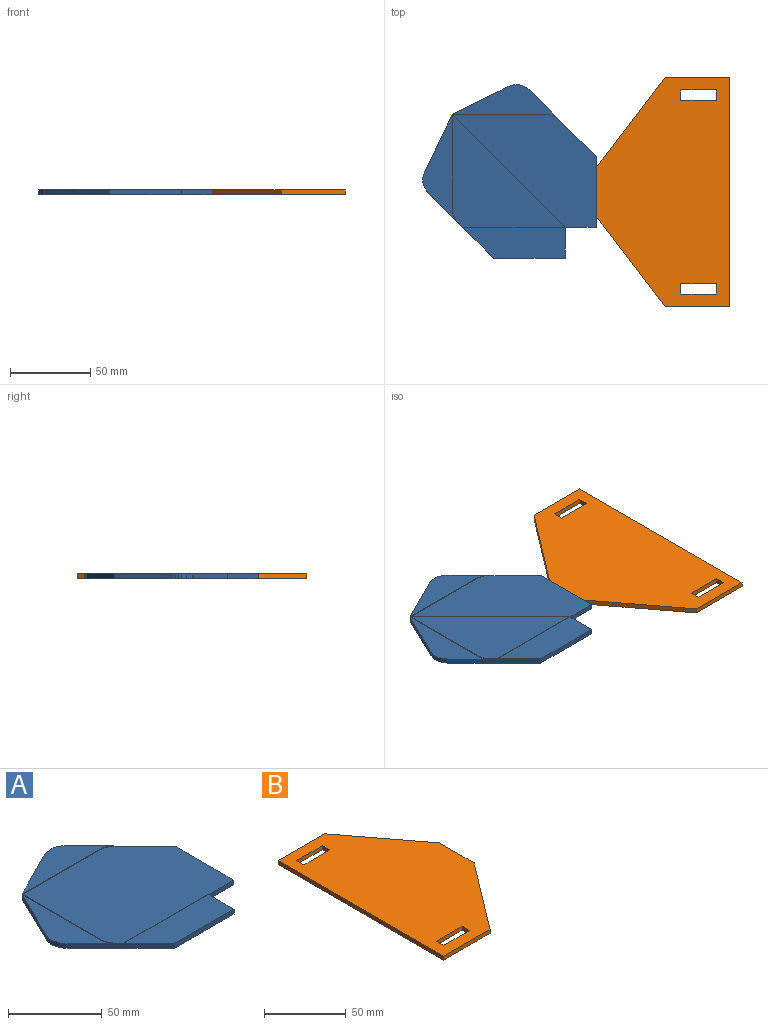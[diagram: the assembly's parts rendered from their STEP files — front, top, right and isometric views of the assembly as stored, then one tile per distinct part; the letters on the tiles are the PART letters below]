
ASSEMBLY  parts=2 mates=1
PART A: 45 faces, bbox 108x108x3.5 mm
  f0: plane 66.76x21.29mm, normal (0,0,1), area 652.9mm2, adj f1,f20,f21,f22,f23,f24,f25,f26
  f1: plane 21.32x21.32mm, normal (-0.71,-0.71,0), area 93mm2, adj f0,f2,f27,f29,f37,f38,f43
  f2: plane 19.19x19.19mm, normal (-0.71,-0.71,0), area 88.2mm2, adj f1,f3,f29,f44
  f3: plane 44.78x3.25mm, normal (0,-1,0), area 145.5mm2, adj f2,f4,f29,f44
  f4: plane 19.19x3.25mm, normal (1,0,0), area 62.4mm2, adj f3,f5,f29,f39,f44
  f5: plane 19.19x3mm, normal (0,-1,0), area 57.6mm2, adj f4,f6,f28,f29
  f6: plane 44.07x3mm, normal (1,0,0), area 132.2mm2, adj f5,f7,f28,f29
  f7: plane 22.74x22.74mm, normal (0.71,0.71,0), area 96.5mm2, adj f6,f8,f28,f29
  f8: plane 3x0.53mm, normal (0.71,0.71,0), area 2.3mm2, adj f7,f9,f28,f29
  f9: plane 17.95x17.94mm, normal (0.71,0.71,0), area 88.8mm2, adj f8,f10,f29,f30,f35
  f10: plane 3.5x0.34mm, normal (0.71,0.71,0), area 1.7mm2, adj f9,f11,f29,f35
  f11: plane 3.5x1.16mm, normal (0.61,0.79,0), area 5.1mm2, adj f10,f12,f29,f35
  f12: plane 3.5x1.95mm, normal (0.51,0.86,0), area 7.9mm2, adj f11,f13,f29,f35
  f13: plane 3.5x2.17mm, normal (0.36,0.93,0), area 8.2mm2, adj f12,f14,f29,f35
  f14: plane 3.5x1.65mm, normal (0.19,0.98,0), area 5.9mm2, adj f13,f15,f29,f35
  f15: plane 3.5x1.43mm, normal (0,1,0), area 5mm2, adj f14,f16,f29,f35
  f16: plane 3.5x2.65mm, normal (-0.13,0.99,0), area 9.4mm2, adj f15,f17,f29,f35
  f17: plane 3.5x2.49mm, normal (-0.32,0.95,0), area 9.2mm2, adj f16,f18,f29,f35
  f18: plane 3.5x0.4mm, normal (-0.51,0.86,0), area 1.6mm2, adj f17,f19,f29,f35
  f19: plane 34.11x17.06mm, normal (-0.45,0.89,0), area 133.5mm2, adj f18,f20,f28,f29,f31,f35,f39,f40
  f20: plane 35.54x17.06mm, normal (-0.9,0.43,0), area 118.3mm2, adj f0,f19,f21,f29
  f21: plane 3x0.3mm, normal (-0.91,0.41,0), area 1mm2, adj f0,f20,f22,f29
  f22: plane 3x2.11mm, normal (-0.94,0.35,0), area 6.8mm2, adj f0,f21,f23,f29
  f23: plane 3x1.91mm, normal (-0.97,0.24,0), area 5.9mm2, adj f0,f22,f24,f29
  f24: plane 3x1.78mm, normal (-1,0,0), area 5.3mm2, adj f0,f23,f25,f29
  f25: plane 3.44x3mm, normal (-0.96,-0.27,0), area 10.7mm2, adj f0,f24,f26,f29
  f26: plane 3.39x3mm, normal (-0.86,-0.52,0), area 11.9mm2, adj f0,f25,f27,f29
  f27: plane 3x0.57mm, normal (-0.72,-0.7,0), area 2.4mm2, adj f0,f1,f26,f29
  f28: plane 89.55x70.37mm, normal (0,0,1), area 3477.1mm2, adj f5,f6,f7,f8,f19,f30,f31,f32
  f29: plane 108.04x108.04mm, normal (0,0,-1), area 8282.6mm2, adj f1,f2,f3,f4,f5,f6,f7,f8
  f30: plane 1.82x1.38mm, normal (-0.6,-0.8,0), area 1.1mm2, adj f9,f28,f34,f35
  f31: plane 57.53x0.5mm, normal (0,-1,0), area 28.8mm2, adj f19,f28,f32,f35
  f32: plane 2.07x0.5mm, normal (-0.05,-1,0), area 1mm2, adj f28,f31,f33,f35
  f33: plane 2.49x0.5mm, normal (-0.19,-0.98,0), area 1.3mm2, adj f28,f32,f34,f35
  f34: plane 2.35x1.07mm, normal (-0.41,-0.91,0), area 1.3mm2, adj f28,f30,f33,f35
  f35: plane 66.26x21.5mm, normal (0,0,1), area 655.4mm2, adj f9,f10,f11,f12,f13,f14,f15,f16
  f36: plane 1.96x1.09mm, normal (-0.87,-0.49,0), area 1.1mm2, adj f0,f37,f42,f43
  f37: plane 1.19x1.03mm, normal (-0.76,-0.65,0), area 0.8mm2, adj f0,f1,f36,f43
  f38: plane 63.97x0.25mm, normal (0,-1,0), area 16mm2, adj f1,f39,f43,f44
  f39: plane 70.36x70.36mm, normal (0.71,0.71,0), area 49.8mm2, adj f4,f19,f28,f38,f43
  f40: plane 58.46x0.5mm, normal (-1,0,0), area 29.2mm2, adj f0,f19,f41,f43
  f41: plane 2.67x0.5mm, normal (-1,-0.06,0), area 1.3mm2, adj f0,f40,f42,f43
  f42: plane 2.48x0.56mm, normal (-0.98,-0.22,0), area 1.3mm2, adj f0,f36,f41,f43
  f43: plane 70.38x70.36mm, normal (0,0,1), area 2453.7mm2, adj f1,f19,f36,f37,f38,f39,f40,f41
  f44: plane 63.97x19.19mm, normal (0,0,1), area 1043.5mm2, adj f2,f3,f4,f38
PART B: 16 faces, bbox 82.9x143x3 mm
  f0: plane 6.35x3mm, normal (-1,0,0), area 19mm2, adj f1,f13,f14,f15
  f1: plane 22.23x3mm, normal (0,1,0), area 66.7mm2, adj f0,f2,f14,f15
  f2: plane 6.35x3mm, normal (1,0,0), area 19mm2, adj f1,f13,f14,f15
  f3: plane 22.23x3mm, normal (0,-1,0), area 66.7mm2, adj f4,f11,f14,f15
  f4: plane 6.35x3mm, normal (-1,0,0), area 19mm2, adj f3,f5,f14,f15
  f5: plane 22.23x3mm, normal (0,1,0), area 66.7mm2, adj f4,f11,f14,f15
  f6: plane 40x3mm, normal (0,1,0), area 120mm2, adj f7,f12,f14,f15
  f7: plane 143x3mm, normal (-1,0,0), area 429mm2, adj f6,f8,f14,f15
  f8: plane 40x3mm, normal (0,-1,0), area 120mm2, adj f7,f9,f14,f15
  f9: plane 56.5x42.85mm, normal (0.8,-0.6,0), area 212.7mm2, adj f8,f10,f14,f15
  f10: plane 30x3mm, normal (1,0,0), area 90mm2, adj f9,f12,f14,f15
  f11: plane 6.35x3mm, normal (1,0,0), area 19mm2, adj f3,f5,f14,f15
  f12: plane 56.5x42.85mm, normal (0.8,0.6,0), area 212.7mm2, adj f6,f10,f14,f15
  f13: plane 22.23x3mm, normal (0,-1,0), area 66.7mm2, adj f0,f2,f14,f15
  f14: plane 143x82.85mm, normal (0,0,1), area 9144.3mm2, adj f0,f1,f2,f3,f4,f5,f6,f7
  f15: plane 143x82.85mm, normal (0,0,-1), area 9144.3mm2, adj f0,f1,f2,f3,f4,f5,f6,f7
PLACE A t=(-46.89,-2.59,-1.75)mm
PLACE B rot(axis=(0,0,1),180deg) t=(165.4,39.82,-1.75)mm
MATE fastened B.f10 <-> A.f6  axis (-1,0,0) through (-28.88,7.84,-1.75)mm
